# Revit family: 0052585 Sylvania Lighting Fixture RANA NEO 3500LM REC 600x600 840 DALI EM 2L WHITE
name_source: partatom
category: Lighting Fixtures
revit_build: Autodesk Revit 2016 (Build: 20150220_1215(x64)
units: mm (PartAtom-declared; Revit-internal decimal feet)

## family parameters
Cut with Voids When Loaded = No
Host = Face
Light Source = Yes
OmniClass Number = 23.80.70.00
OmniClass Title = Lighting
Part Type = Normal
Room Calculation Point = No
Round Connector Dimension = Use Diameter
Shared = No

## types (1)
- 0052585 RANA NEO 3500LM R 600 840 DALI EM 2L WHT
    1200_SYL = No
    1Ref_SYL = No
    2Ref_SYL = Yes
    600x600_SYL = Yes
    625x625_SYL = No
    Apparent Load = 33 VA
    Assembly Code = D5020200
    AssetType = Fixed
    ClassificationName = Uniclass2015
    ClassificationValue = EF_70_80
    Color Filter = 16777215
    Cost = 0 $
    Default Elevation = 1219 mm
    Description = -
    Dimming Lamp Color Temperature Shift = <None>
    DocumentationLiterature = http://www.sylvania-lighting.com
    ElectricShockClassification = 106
    Emit Shape Visible in Rendering = No
    Emit from Rectangle Length = 542 mm  [stored 1.77822 ft]
    Emit from Rectangle Width = 282 mm
    Height = 52 mm
    IfcExportAs = Class I
    IfcExportType = IfcLightFixtureType
    ImpactProtectionIndex = IfcLightFixtureType
    IngressProtection = IfcLightFixtureType
    InputNominalFrequency = 4000
    InputVoltage = 0
    Inset_SYL = 20 mm  [stored 0.0656168 ft]
    LED Length = 568 mm  [stored 1.86352 ft]
    LED Width = 290 mm  [stored 0.951444 ft]
    LED inner void = 522 mm
    LED inside width = 165 mm  [stored 0.541339 ft]
    LampColourRenderingIndex = 16500
    LampColourTemperature = LED
    LampMacAdamStep = 80
    LampNominalLuminous = 4000 K
    Length_SYL = 595 mm  [stored 1.9521 ft]
    LightOutputRatio = LED
    LouverNumber_SYL = 14
    LuminaireType = 0
    ManufacturerName = 106 lm/W
    Material = Feilo Sylvania
    Material_1_SYL = <By Category>
    Material_2_SYL = <By Category>
    Material_3_SYL = <By Category>
    Material_4_SYL = <By Category>
    Model = RANA NEO 3500LM REC 600x600 840 DALI EM 2L WHITE
    ModelNumber = 0052585
    ModelReference = RANA NEO 3500LM REC 600x600 840 DALI EM 2L WHITE
    Name = RANA NEO 3500LM REC 600x600 840 DALI EM 2L WHITE
    NominalDepth = 595 mm  [stored 1.9521 ft]
    NominalHeight = 60 mm  [stored 0.19685 ft]
    NominalLength = 595 mm  [stored 1.9521 ft]
    Photometric Web File = 0052585.ies
    PowerConsumption = Lighting
    PowerFactor = 0.95
    ReflectorInset_SYL = 30 mm  [stored 0.0984252 ft]
    ReflectorLength_SYL = 550 mm
    ReflectorNumber_SYL = 2
    SlopeBottomWidth_SYL = 593 mm  [stored 1.94554 ft]
    SlopeHeight_SYL = 17 mm
    SlopeTopWidth_SYL = 410 mm  [stored 1.34514 ft]
    Tilt Angle = -90.00°
    TopWidth_SYL = 295 mm  [stored 0.967848 ft]
    Type Image = <None>
    TypeName = RANA NEO 3500LM REC 600x600 840 DALI EM 2L WHITE
    URL = 0.96
    Voltage = 0 V
    WarrantyDescription = http://www.sylvania-lighting.com
    Width_SYL = 595 mm  [stored 1.9521 ft]
    fin 1 = 480 mm  [stored 1.5748 ft]
    fin 2 = 407 mm  [stored 1.3353 ft]
    fin 4 = 258 mm  [stored 0.846457 ft]
    fin 5 = 185 mm  [stored 0.606955 ft]
    fin 6 = 110 mm  [stored 0.360892 ft]
    fin3 = 332 mm  [stored 1.08924 ft]
    fin7 = 37 mm  [stored 0.121391 ft]

note: [stored X ft] marks values corroborated as IEEE doubles in the binary element streams (Revit-internal decimal feet)

## geometry (parser evidence)
native form markers: Sweep x9
no freeform markers — native parametric forms only
